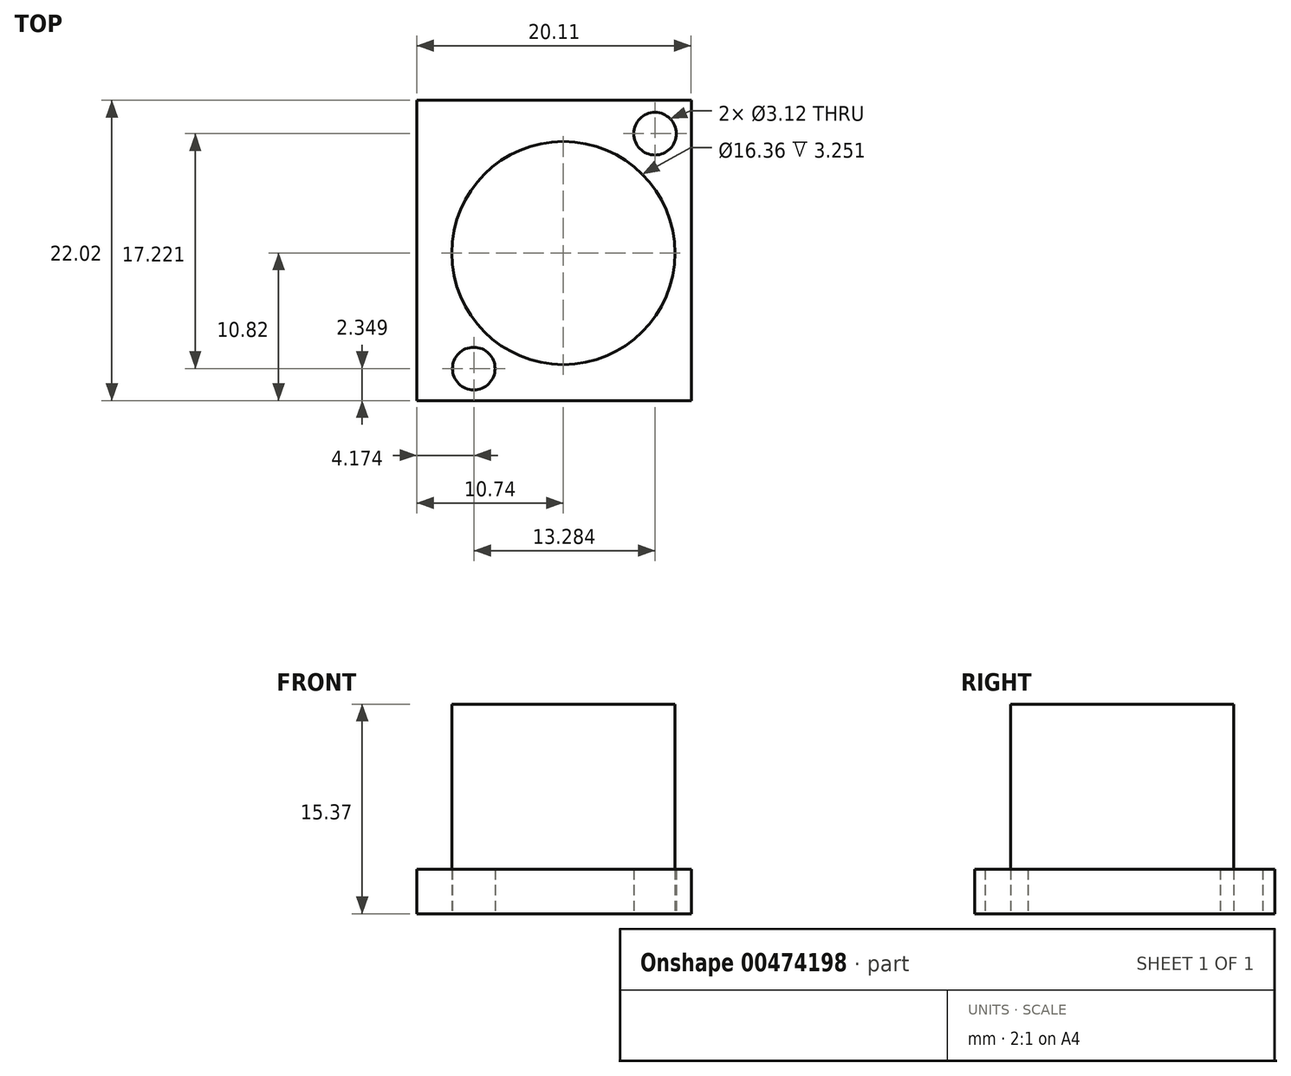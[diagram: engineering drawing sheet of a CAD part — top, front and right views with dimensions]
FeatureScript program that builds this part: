
annotation { "Feature Type Name" : "Feature", "Feature Type Description" : "" }
export const myFeature = defineFeature(function(context is Context, id is Id, definition is map)
    precondition{}
    {
        {
            var Q0;
            Q0=qCreatedBy(makeId("Top.planeOp"),FACE);
            var sketch = newSketch(context, id + "F0", { "sketchPlane" : qUnion([Q0])});
            skCircle(sketch, "E0", {"center": v(0, 0) * mm, "radius": 8.18 * mm});
            skLineSegment(sketch, "E1.bottom", {"start": v(-10.74, 11.2) * mm, "end": v(9.37, 11.2) * mm});
            skLineSegment(sketch, "E1.top", {"start": v(-10.74, -10.82) * mm, "end": v(9.37, -10.82) * mm});
            skLineSegment(sketch, "E1.left", {"start": v(-10.74, 11.2) * mm, "end": v(-10.74, -10.82) * mm});
            skLineSegment(sketch, "E1.right", {"start": v(9.37, 11.2) * mm, "end": v(9.37, -10.82) * mm});
            skSolve(sketch);
        }
        {
            var Q0;
            Q0=qCreatedBy(makeId("Top.planeOp"),FACE);
            var sketch = newSketch(context, id + "F1", { "sketchPlane" : qUnion([Q0])});
            skCircle(sketch, "E2", {"center": v(6.72, 8.75) * mm, "radius": 1.56 * mm});
            skCircle(sketch, "E3", {"center": v(-6.57, -8.47) * mm, "radius": 1.56 * mm});
            skSolve(sketch);
        }
        {
            var Q0;
            Q0=makeQuery(id+"F0.imprint","IMPRINT",FACE,{"disambiguationData":[TD([[makeQuery(id+"F0.imprint","IMPRINT",EDGE,{"derivedFrom":sQuery(id+"F0.wireOp",EDGE,"E0")}),1.0]])]});
            var Q1;
            Q1=sQuery(id+"F0.wireOp",EDGE,"E0");
            extrude(context, id + "F2", {"entities" : qUnion([Q0]), "surfaceEntities" : qUnion([Q1]), "depth" : 15.37 * mm});
        }
        {
            var Q0;
            Q0=makeQuery(id+"F0.imprint","IMPRINT",FACE,{"disambiguationData":[TD([[makeQuery(id+"F0.imprint","IMPRINT",EDGE,{"derivedFrom":sQuery(id+"F0.wireOp",EDGE,"E0")}),-1.0]])]});
            extrude(context, id + "F3", {"entities" : qUnion([Q0]), "depth" : 3.25 * mm});
        }
        {
            var Q0;
            Q0=makeQuery(id+"F1.imprint","IMPRINT",FACE,{"disambiguationData":[TD([[makeQuery(id+"F1.imprint","IMPRINT",EDGE,{"derivedFrom":sQuery(id+"F1.wireOp",EDGE,"E2")}),1.0]])]});
            extrude(context, id + "F4", {"entities" : qUnion([Q0]), "operationType" : NewBodyOperationType.REMOVE, "oppositeDirection" : true, "depth" : 1.63 * mm});
        }
        {
            var Q0;
            Q0=makeQuery(id+"F1.imprint","IMPRINT",FACE,{"disambiguationData":[TD([[makeQuery(id+"F1.imprint","IMPRINT",EDGE,{"derivedFrom":sQuery(id+"F1.wireOp",EDGE,"E3")}),1.0]])]});
            extrude(context, id + "F5", {"entities" : qUnion([Q0]), "operationType" : NewBodyOperationType.REMOVE, "depth" : 3.25 * mm});
        }
        {
            var Q0;
            Q0=makeQuery(id+"F1.imprint","IMPRINT",FACE,{"disambiguationData":[TD([[makeQuery(id+"F1.imprint","IMPRINT",EDGE,{"derivedFrom":sQuery(id+"F1.wireOp",EDGE,"E2")}),1.0]])]});
            extrude(context, id + "F6", {"entities" : qUnion([Q0]), "operationType" : NewBodyOperationType.REMOVE, "depth" : 3.25 * mm});
        }
    });
